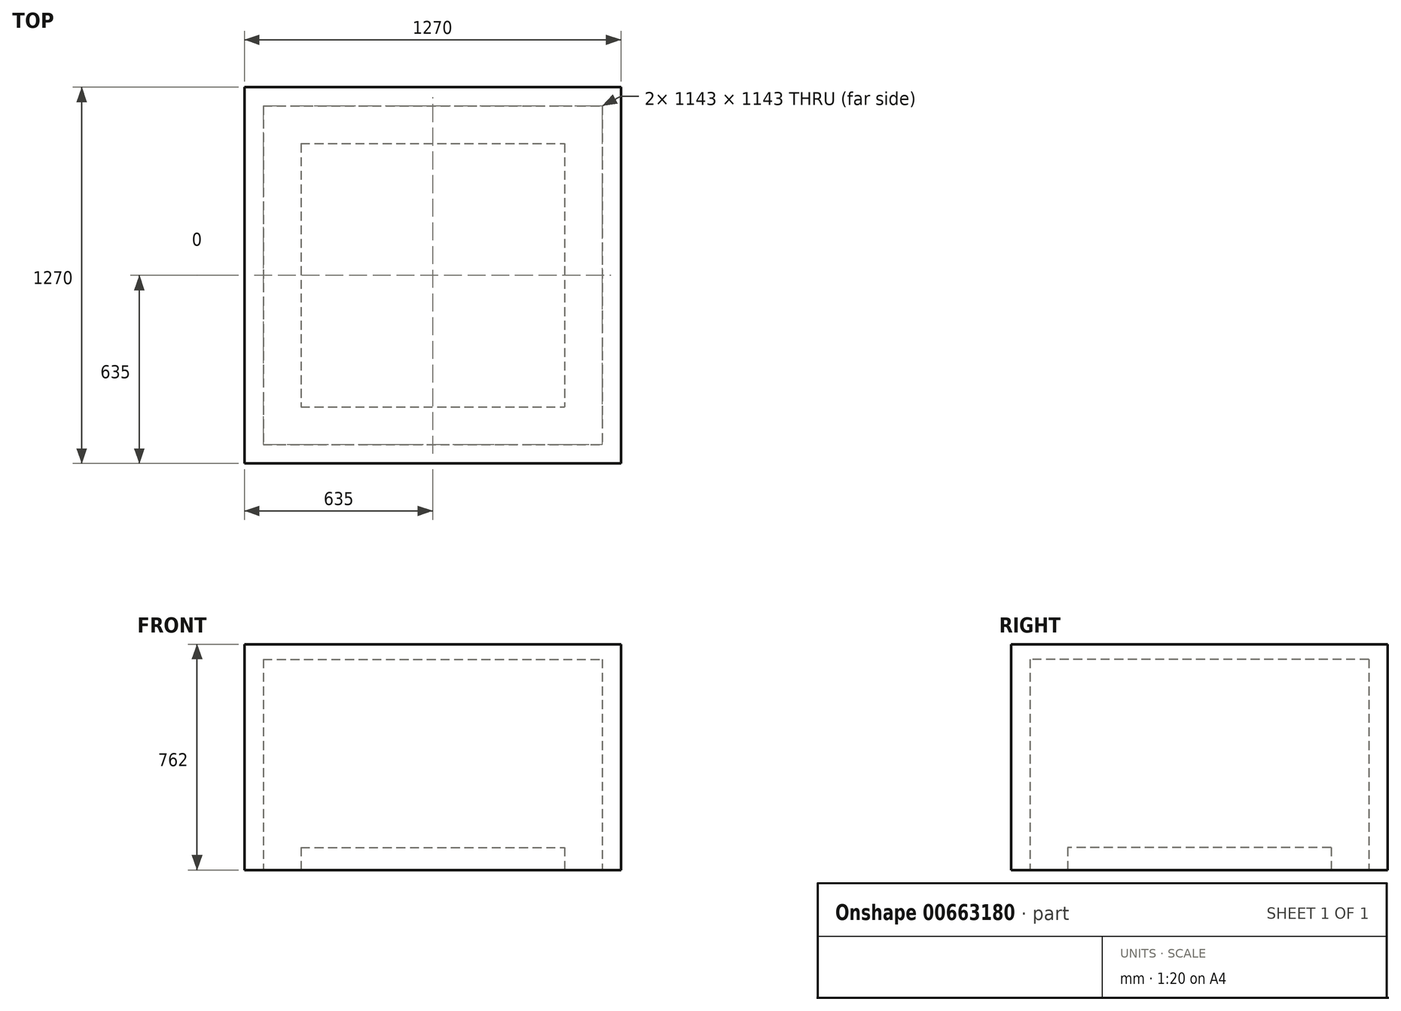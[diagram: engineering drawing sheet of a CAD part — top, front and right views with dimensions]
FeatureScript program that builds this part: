
annotation { "Feature Type Name" : "Feature", "Feature Type Description" : "" }
export const myFeature = defineFeature(function(context is Context, id is Id, definition is map)
    precondition{}
    {
        {
            var Q0;
            Q0=qCreatedBy(makeId("Top.planeOp"),FACE);
            var sketch = newSketch(context, id + "F0", { "sketchPlane" : qUnion([Q0])});
            skLineSegment(sketch, "E0.bottom", {"start": v(-635, 635) * mm, "end": v(635, 635) * mm});
            skLineSegment(sketch, "E0.top", {"start": v(-635, -635) * mm, "end": v(635, -635) * mm});
            skLineSegment(sketch, "E0.left", {"start": v(-635, 635) * mm, "end": v(-635, -635) * mm});
            skLineSegment(sketch, "E0.right", {"start": v(635, 635) * mm, "end": v(635, -635) * mm});
            skPoint(sketch, "E0.middle", {"position": v(0, 0) * mm});
            skSolve(sketch);
        }
        {
            var Q0;
            Q0 = qSketchRegion(id + "F0", true);
            extrude(context, id + "F1", {"entities" : qUnion([Q0]), "depth" : 762 * mm, "offsetDistance" : 25.4 * mm});
        }
        {
            var Q0;
            Q0=makeQuery(id+"F1.opExtrude","CAP_FACE",FACE,{"disambiguationData":[OSD([sQuery(id+"F0.wireOp",EDGE,"E0.bottom"),sQuery(id+"F0.wireOp",EDGE,"E0.top"),sQuery(id+"F0.wireOp",EDGE,"E0.left"),sQuery(id+"F0.wireOp",EDGE,"E0.right")])],"isStart":true});
            var sketch = newSketch(context, id + "F2", { "sketchPlane" : qUnion([Q0])});
            skLineSegment(sketch, "E1.bottom", {"start": v(-571.5, -571.5) * mm, "end": v(571.5, -571.5) * mm});
            skLineSegment(sketch, "E1.top", {"start": v(-571.5, 571.5) * mm, "end": v(571.5, 571.5) * mm});
            skLineSegment(sketch, "E1.left", {"start": v(-571.5, -571.5) * mm, "end": v(-571.5, 571.5) * mm});
            skLineSegment(sketch, "E1.right", {"start": v(571.5, -571.5) * mm, "end": v(571.5, 571.5) * mm});
            skPoint(sketch, "E1.middle", {"position": v(0, 0) * mm});
            skSolve(sketch);
        }
        {
            var Q0;
            Q0=makeQuery(id+"F2.imprint","IMPRINT",FACE,{"disambiguationData":[TD([[makeQuery(id+"F2.imprint","IMPRINT",EDGE,{"derivedFrom":sQuery(id+"F2.wireOp",EDGE,"E1.bottom")}),1.0]])]});
            extrude(context, id + "F3", {"entities" : qUnion([Q0]), "operationType" : NewBodyOperationType.REMOVE, "oppositeDirection" : true, "depth" : 711.2 * mm, "offsetDistance" : 25.4 * mm});
        }
        {
            var Q0;
            Q0=makeQuery(id+"F1.opExtrude","CAP_FACE",FACE,{"disambiguationData":[OSD([sQuery(id+"F0.wireOp",EDGE,"E0.bottom"),sQuery(id+"F0.wireOp",EDGE,"E0.top"),sQuery(id+"F0.wireOp",EDGE,"E0.left"),sQuery(id+"F0.wireOp",EDGE,"E0.right")])],"isStart":true});
            var sketch = newSketch(context, id + "F4", { "sketchPlane" : qUnion([Q0])});
            skLineSegment(sketch, "E2.bottom", {"start": v(-444.5, -444.5) * mm, "end": v(444.5, -444.5) * mm});
            skLineSegment(sketch, "E2.top", {"start": v(-444.5, 444.5) * mm, "end": v(444.5, 444.5) * mm});
            skLineSegment(sketch, "E2.left", {"start": v(-444.5, -444.5) * mm, "end": v(-444.5, 444.5) * mm});
            skLineSegment(sketch, "E2.right", {"start": v(444.5, -444.5) * mm, "end": v(444.5, 444.5) * mm});
            skPoint(sketch, "E2.middle", {"position": v(0, 0) * mm});
            skSolve(sketch);
        }
        {
            var Q0;
            Q0=makeQuery(id+"F4.imprint","IMPRINT",FACE,{"disambiguationData":[TD([[makeQuery(id+"F4.imprint","IMPRINT",EDGE,{"derivedFrom":sQuery(id+"F4.wireOp",EDGE,"E2.bottom")}),1.0]])]});
            extrude(context, id + "F5", {"entities" : qUnion([Q0]), "oppositeDirection" : true, "depth" : 76.2 * mm, "offsetDistance" : 25.4 * mm});
        }
    });
